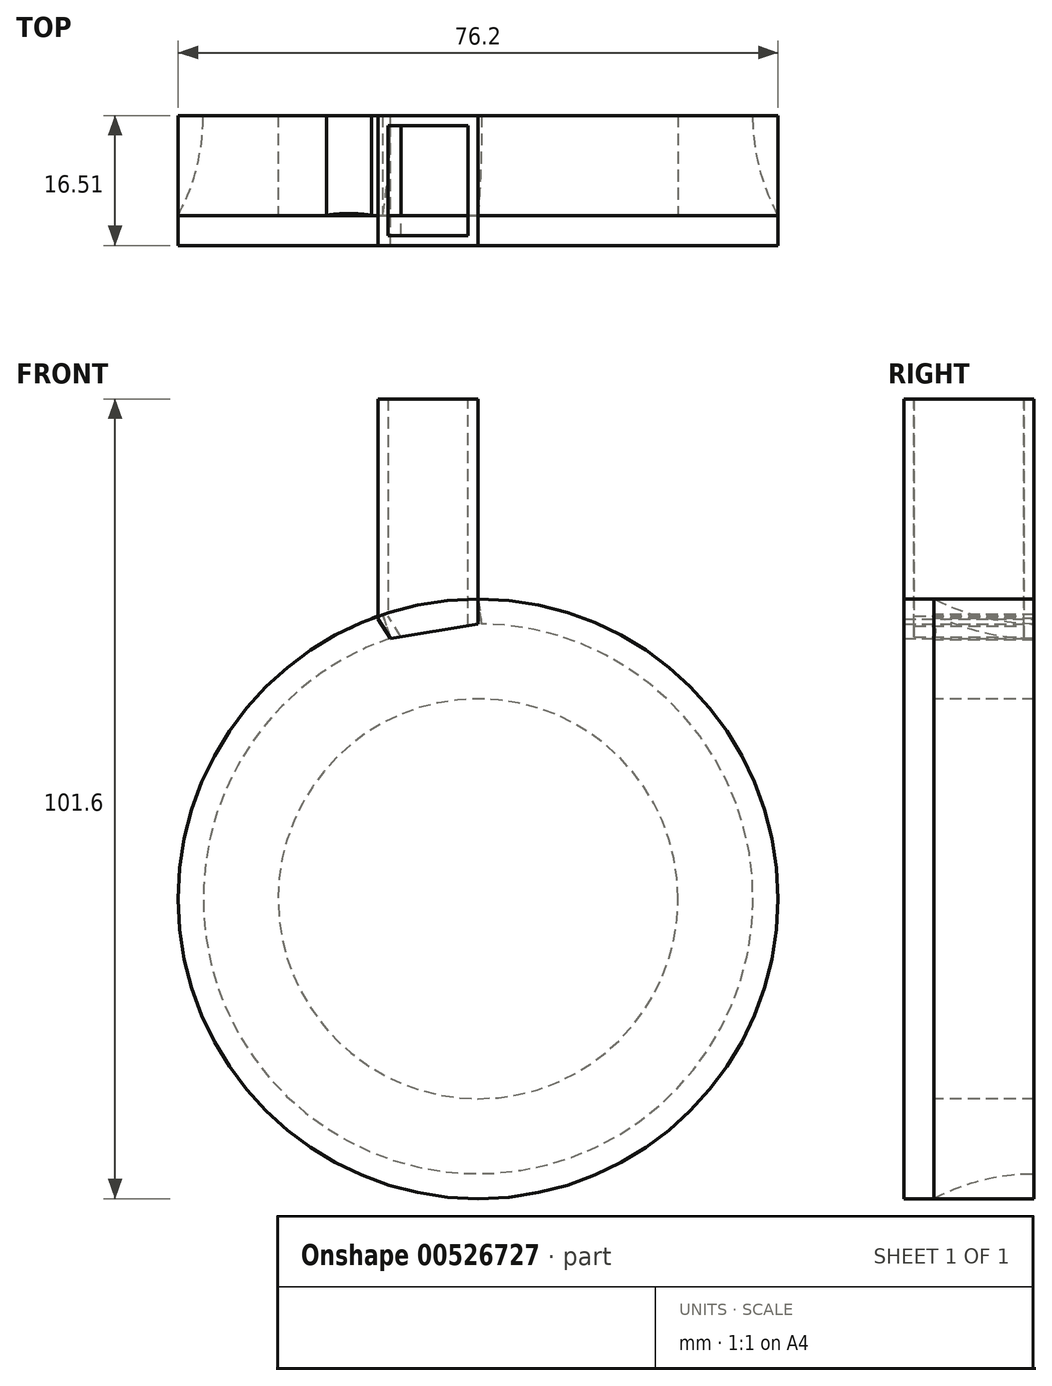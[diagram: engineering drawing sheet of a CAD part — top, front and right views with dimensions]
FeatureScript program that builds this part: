
annotation { "Feature Type Name" : "Feature", "Feature Type Description" : "" }
export const myFeature = defineFeature(function(context is Context, id is Id, definition is map)
    precondition{}
    {
        {
            var Q0;
            Q0=qCreatedBy(makeId("Front.planeOp"),FACE);
            var sketch = newSketch(context, id + "F0", { "sketchPlane" : qUnion([Q0])});
            skCircle(sketch, "E0", {"center": v(0, 0) * mm, "radius": 25.4 * mm});
            skArc(sketch, "E1", {"start": v(-11.12, 33.1) * mm, "mid": v(5.41, -34.5) * mm, "end": v(0.45, 34.92) * mm});
            skArc(sketch, "E2", {"start": v(-19.28, 32.86) * mm, "mid": v(10, -36.77) * mm, "end": v(0, 38.1) * mm});
            skFitSpline(sketch, "E3", {"points": [v(-13.56, 35.6) * mm, v(-19.28, 32.86) * mm], "startDerivative": vector(-5.73, -2.75) * mm, "endDerivative": vector(-5.73, -2.75) * mm});
            skLineSegment(sketch, "E4", {"start": v(0, 38.1) * mm, "end": v(1.79, 25.34) * mm});
            skLineSegment(sketch, "E5", {"start": v(-8.09, 24.08) * mm, "end": v(-12.13, 36.12) * mm});
            skArc(sketch, "E6.trimOffspring", {"start": v(-12.13, 36.12) * mm, "mid": v(-12.85, 35.87) * mm, "end": v(-13.56, 35.6) * mm});
            skSolve(sketch);
        }
        {
            var Q0;
            Q0=makeQuery(id+"F0.imprint","IMPRINT",FACE,{"disambiguationData":[TD([[makeQuery(id+"F0.imprint","IMPRINT",EDGE,{"derivedFrom":sQuery(id+"F0.wireOp",EDGE,"E0")}),1.0]])]});
            var Q1;
            Q1=makeQuery(id+"F0.imprint","IMPRINT",FACE,{"disambiguationData":[TD([[makeQuery(id+"F0.imprint","IMPRINT",EDGE,{"derivedFrom":sQuery(id+"F0.wireOp",EDGE,"E1")}),-1.0]])]});
            extrude(context, id + "F1", {"entities" : qUnion([Q0, Q1]), "oppositeDirection" : true, "depth" : 12.7 * mm, "offsetDistance" : 25.4 * mm});
        }
        {
            var Q0;
            Q0=qCreatedBy(makeId("Front.planeOp"),FACE);
            var sketch = newSketch(context, id + "F2", { "sketchPlane" : qUnion([Q0])});
            skCircle(sketch, "E7", {"center": v(0, 0) * mm, "radius": 38.1 * mm});
            skSolve(sketch);
        }
        {
            var Q0;
            Q0 = qSketchRegion(id + "F2", true);
            extrude(context, id + "F3", {"entities" : qUnion([Q0]), "depth" : 3.8 * mm, "offsetDistance" : 25.4 * mm});
        }
        {
            var Q0;
            Q0=makeQuery(id+"F1.opExtrude","CAP_EDGE",EDGE,{"disambiguationData":[OSD([sQuery(id+"F0.wireOp",EDGE,"E1")])],"isStart":true});
            fillet(context, id + "F4", {"entities" : qUnion([Q0]), "radius" : 26.98 * mm, "tangentPropagation" : true, "allowEdgeOverflow" : false});
        }
        {
            var Q0;
            Q0=qCreatedBy(makeId("Front.planeOp"),FACE);
            var sketch = newSketch(context, id + "F5", { "sketchPlane" : qUnion([Q0])});
            skLineSegment(sketch, "E8", {"start": v(0, 0) * mm, "end": v(0, 38.1) * mm});
            skLineSegment(sketch, "E9", {"start": v(0, 0) * mm, "end": v(-12.7, 0) * mm});
            skLineSegment(sketch, "E10", {"start": v(-12.7, 0) * mm, "end": v(-12.7, 35.56) * mm});
            skLineSegment(sketch, "E11", {"start": v(-12.7, 35.56) * mm, "end": v(0, 38.1) * mm});
            skLineSegment(sketch, "E12", {"start": v(0, 38.1) * mm, "end": v(0, 63.5) * mm});
            skLineSegment(sketch, "E13", {"start": v(0, 63.5) * mm, "end": v(-12.7, 63.5) * mm});
            skLineSegment(sketch, "E14", {"start": v(-12.7, 63.5) * mm, "end": v(-12.7, 35.56) * mm});
            skLineSegment(sketch, "E15", {"start": v(0, 38.1) * mm, "end": v(0.63, 34.97) * mm});
            skLineSegment(sketch, "E16", {"start": v(0.63, 34.97) * mm, "end": v(-11.12, 33.04) * mm});
            skLineSegment(sketch, "E17", {"start": v(-11.12, 33.04) * mm, "end": v(-12.7, 35.56) * mm});
            skSolve(sketch);
        }
        {
            var Q0;
            Q0=makeQuery(id+"F5.imprint","IMPRINT",FACE,{"disambiguationData":[TD([[makeQuery(id+"F5.imprint","IMPRINT",EDGE,{"derivedFrom":sQuery(id+"F5.wireOp",EDGE,"E11")}),1.0]])]});
            var Q1;
            {var subQ0=sQuery(id+"F5.wireOp",EDGE,"E11");Q1=makeQuery(id+"F5.imprint","IMPRINT",FACE,{"disambiguationData":[TD([[makeQuery(id+"F5.imprint","IMPRINT",EDGE,{"derivedFrom":subQ0}),-1.0]])]});}
            extrude(context, id + "F6", {"entities" : qUnion([Q0, Q1]), "depth" : 3.8 * mm, "offsetDistance" : 25.4 * mm, "hasSecondDirection" : true, "secondDirectionOppositeDirection" : true, "secondDirectionDepth" : 12.7 * mm});
        }
        {
            var Q0;
            Q0=makeQuery(id+"F6.opExtrude","SWEPT_FACE",FACE,{"disambiguationData":[OSD([sQuery(id+"F5.wireOp",EDGE,"E13")])]});
            var Q1;
            Q1=makeQuery(id+"F6.opExtrude","SWEPT_FACE",FACE,{"disambiguationData":[OSD([sQuery(id+"F5.wireOp",EDGE,"E16")])]});
            shell(context, id + "F7", {"entities" : qUnion([Q0, Q1]), "thickness" : 1.27 * mm});
        }
    });
